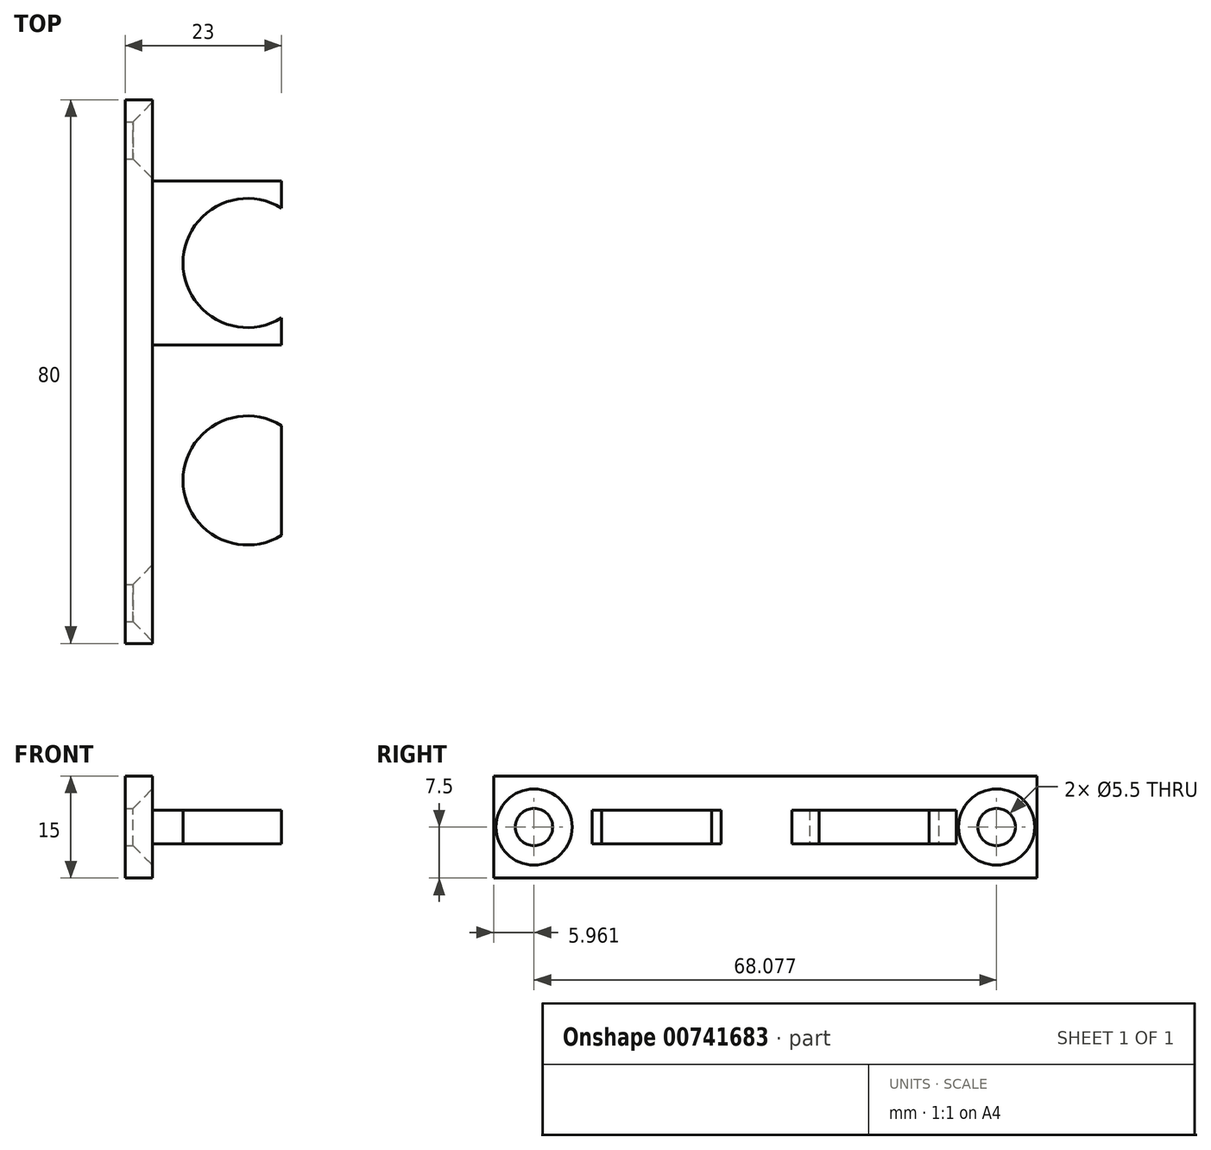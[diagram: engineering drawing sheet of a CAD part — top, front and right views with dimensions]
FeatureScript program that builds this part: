
annotation { "Feature Type Name" : "Feature", "Feature Type Description" : "" }
export const myFeature = defineFeature(function(context is Context, id is Id, definition is map)
    precondition{}
    {
        {
            var Q0;
            Q0=qCreatedBy(makeId("Top.planeOp"),FACE);
            var sketch = newSketch(context, id + "F0", { "sketchPlane" : qUnion([Q0])});
            skLineSegment(sketch, "E0.bottom", {"start": v(2, 40) * mm, "end": v(-2, 40) * mm});
            skLineSegment(sketch, "E0.top", {"start": v(2, -40) * mm, "end": v(-2, -40) * mm});
            skLineSegment(sketch, "E0.left", {"start": v(2, 40) * mm, "end": v(2, -40) * mm});
            skLineSegment(sketch, "E0.right", {"start": v(-2, 40) * mm, "end": v(-2, -40) * mm});
            skPoint(sketch, "E0.middle", {"position": v(0, 0) * mm});
            skLineSegment(sketch, "E1.bottom", {"start": v(2, 40) * mm, "end": v(21, 40) * mm});
            skLineSegment(sketch, "E1.top", {"start": v(2, -40) * mm, "end": v(21, -40) * mm});
            skLineSegment(sketch, "E1.right", {"start": v(21, 40) * mm, "end": v(21, -40) * mm});
            skPoint(sketch, "E2", {"position": v(16, 16) * mm});
            skLineSegment(sketch, "E3", {"start": v(21, 0) * mm, "end": v(-2, 0) * mm, "construction": true});
            skPoint(sketch, "E4.MirrorP", {"position": v(16, -16) * mm});
            skArc(sketch, "E5", {"start": v(21, 24.08) * mm, "mid": v(6.5, 16) * mm, "end": v(21, 7.92) * mm});
            skArc(sketch, "E6.MirrorCS", {"start": v(21, -24.08) * mm, "mid": v(6.5, -16) * mm, "end": v(21, -7.92) * mm});
            skLineSegment(sketch, "E7.top", {"start": v(2, -28.08) * mm, "end": v(21, -28.08) * mm});
            skLineSegment(sketch, "E7.left", {"start": v(2, -40) * mm, "end": v(2, -28.08) * mm});
            skLineSegment(sketch, "E7.right", {"start": v(21, -40) * mm, "end": v(21, -28.08) * mm});
            skLineSegment(sketch, "E8.MirrorCS", {"start": v(2, 28.08) * mm, "end": v(21, 28.08) * mm});
            skLineSegment(sketch, "E9", {"start": v(2, 3.92) * mm, "end": v(21, 3.92) * mm});
            skLineSegment(sketch, "E10.MirrorCS", {"start": v(2, -3.92) * mm, "end": v(21, -3.92) * mm});
            skSolve(sketch);
        }
        {
            var Q0;
            {var subQ6=sQuery(id+"F0.wireOp",EDGE,"E0.bottom");Q0=makeQuery(id+"F0.imprint","IMPRINT",FACE,{"disambiguationData":[TD([[makeQuery(id+"F0.imprint","IMPRINT",EDGE,{"derivedFrom":subQ6}),1.0]])]});}
            extrude(context, id + "F1", {"entities" : qUnion([Q0]), "endBound" : BoundingType.SYMMETRIC, "depth" : 15 * mm, "offsetDistance" : 25 * mm});
        }
        {
            var Q0;
            {var subQ0=sQuery(id+"F0.wireOp",EDGE,"E5");Q0=makeQuery(id+"F0.imprint","IMPRINT",FACE,{"disambiguationData":[TD([[makeQuery(id+"F0.imprint","IMPRINT",EDGE,{"derivedFrom":subQ0}),-1.0]])]});}
            var Q1;
            {var subQ0=sQuery(id+"F0.wireOp",EDGE,"E6.MirrorCS");Q1=makeQuery(id+"F0.imprint","IMPRINT",FACE,{"disambiguationData":[TD([[makeQuery(id+"F0.imprint","IMPRINT",EDGE,{"derivedFrom":subQ0}),1.0]])]});}
            extrude(context, id + "F2", {"entities" : qUnion([Q0, Q1]), "operationType" : NewBodyOperationType.ADD, "endBound" : BoundingType.SYMMETRIC, "depth" : 5 * mm, "offsetDistance" : 25 * mm});
        }
        {
            var Q0;
            Q0=makeQuery(id+"F1.opExtrude","SWEPT_FACE",FACE,{"disambiguationData":[OSD([sQuery(id+"F0.wireOp",EDGE,"E0.left")])]});
            var sketch = newSketch(context, id + "F3", { "sketchPlane" : qUnion([Q0])});
            skLineSegment(sketch, "E11", {"start": v(0, 7.5) * mm, "end": v(0, -7.5) * mm, "construction": true});
            skPoint(sketch, "E12", {"position": v(-34.04, 0) * mm});
            skPoint(sketch, "E13.MirrorP", {"position": v(34.04, 0) * mm});
            skSolve(sketch);
        }
        {
            var Q0;
            Q0=sQuery(id+"F3.wireOp",VERTEX,"E12");
            var Q1;
            Q1=sQuery(id+"F3.wireOp",VERTEX,"E13.MirrorP");
            var Q2;
            Q2=makeQuery(id+"F1.opExtrude","SWEPT_BODY",BODY,{"disambiguationData":[OSD([sQuery(id+"F0.wireOp",EDGE,"E0.bottom"),sQuery(id+"F0.wireOp",EDGE,"E0.top"),sQuery(id+"F0.wireOp",EDGE,"E0.left"),sQuery(id+"F0.wireOp",EDGE,"E0.right")])]});
            hole(context, id + "F4", {"style" : HoleStyle.C_SINK, "endStyle" : HoleEndStyle.BLIND, "standardTappedOrClearance" : lookupTablePath({ "standard" : "ISO", "fit" : "Normal", "size" : "M5", "type" : "Clearance" }), "standardBlindInLast" : lookupTablePath({ "fit" : "Standard", "standard" : "ISO", "size" : "M5", "type" : "Clearance" }), "holeDiameter" : 5.5 * mm, "cSinkDiameter" : 11.2 * mm, "cSinkAngle" : 90 * degree, "majorDiameter" : 5 * mm, "holeDepth" : 8 * mm, "isTappedThrough" : true, "tappedDepth" : 8 * mm, "tapClearance" : 0, "startFromSketch" : true, "locations" : qUnion([Q0, Q1]), "scope" : qUnion([Q2])});
        }
    });
